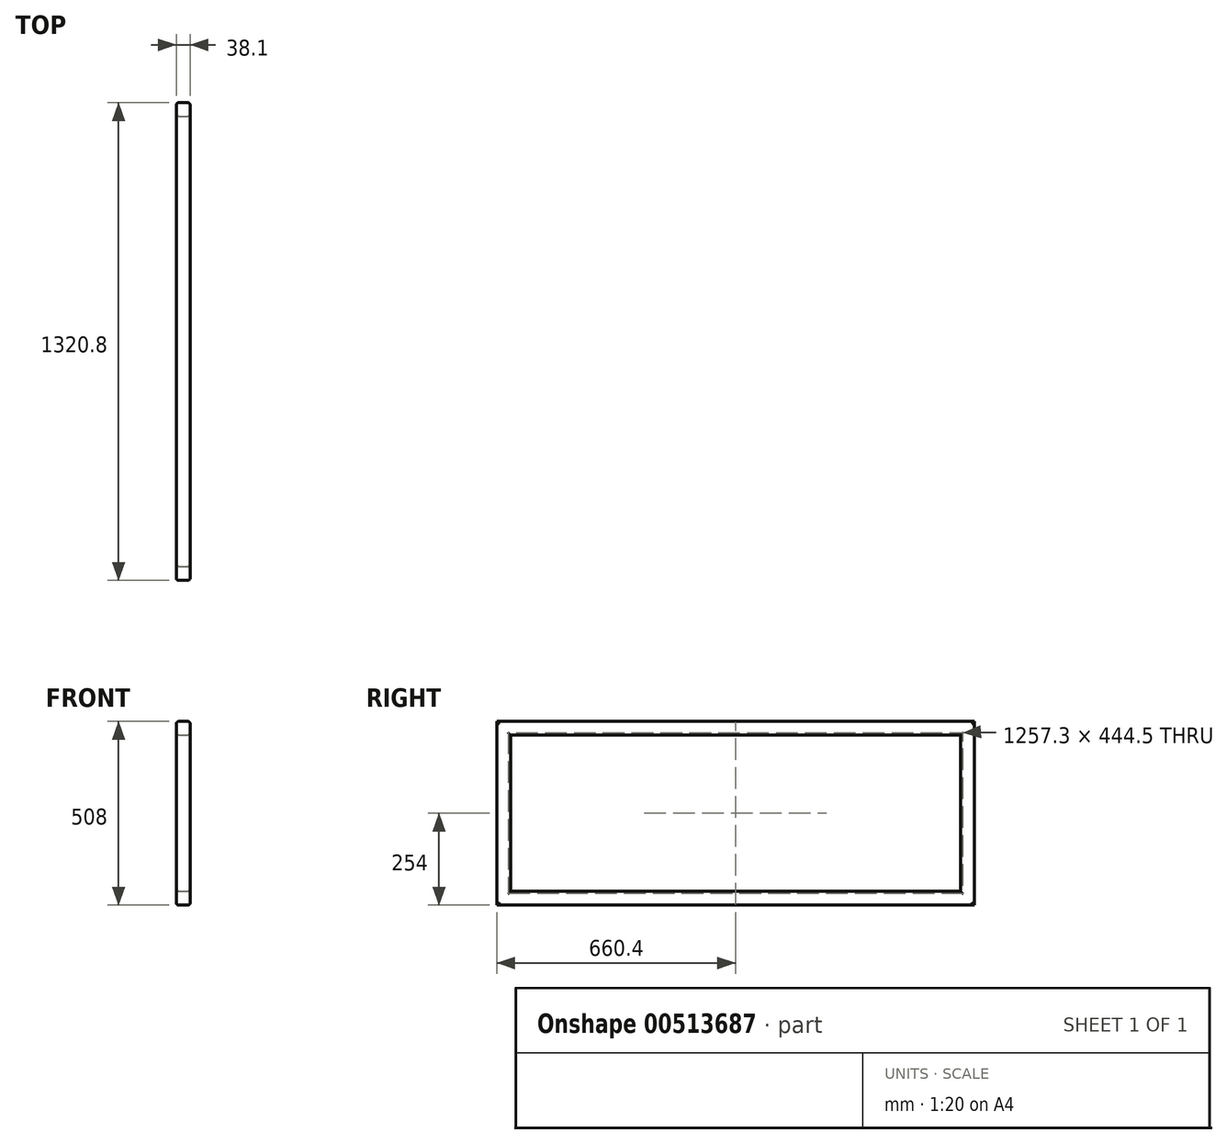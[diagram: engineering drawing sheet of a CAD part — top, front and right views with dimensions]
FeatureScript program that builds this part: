
annotation { "Feature Type Name" : "Feature", "Feature Type Description" : "" }
export const myFeature = defineFeature(function(context is Context, id is Id, definition is map)
    precondition{}
    {
        {
            var Q0;
            Q0=qCreatedBy(makeId("Right.planeOp"),FACE);
            var sketch = newSketch(context, id + "F0", { "sketchPlane" : qUnion([Q0])});
            skLineSegment(sketch, "E0.bottom", {"start": v(-660.4, 254) * mm, "end": v(660.4, 254) * mm});
            skLineSegment(sketch, "E0.top", {"start": v(-660.4, -254) * mm, "end": v(660.4, -254) * mm});
            skLineSegment(sketch, "E0.left", {"start": v(-660.4, 254) * mm, "end": v(-660.4, -254) * mm});
            skLineSegment(sketch, "E0.right", {"start": v(660.4, 254) * mm, "end": v(660.4, -254) * mm});
            skPoint(sketch, "E0.middle", {"position": v(0, 0) * mm});
            skSolve(sketch);
        }
        {
            var Q0;
            Q0=qCreatedBy(makeId("Front.planeOp"),FACE);
            var sketch = newSketch(context, id + "F1", { "sketchPlane" : qUnion([Q0])});
            skPoint(sketch, "E1.0", {"position": v(0, -254) * mm});
            skLineSegment(sketch, "E2", {"start": v(0, -254) * mm, "end": v(-12.7, -254) * mm});
            skLineSegment(sketch, "E3", {"start": v(-19.05, -247.65) * mm, "end": v(-19.05, -222.25) * mm});
            skLineSegment(sketch, "E4", {"start": v(-12.7, -215.9) * mm, "end": v(0, -215.9) * mm});
            skLineSegment(sketch, "E5.0", {"start": v(-12.7, -219.08) * mm, "end": v(0, -219.08) * mm});
            skLineSegment(sketch, "E5.1", {"start": v(-15.88, -247.65) * mm, "end": v(-15.88, -222.25) * mm});
            skLineSegment(sketch, "E5.2", {"start": v(0, -250.83) * mm, "end": v(-12.7, -250.83) * mm});
            skPoint(sketch, "E6.visualSharp", {"position": v(-15.88, -219.08) * mm});
            skArc(sketch, "E6.filletArc", {"start": v(-12.7, -219.08) * mm, "mid": v(-14.95, -220) * mm, "end": v(-15.88, -222.25) * mm});
            skPoint(sketch, "E7.visualSharp", {"position": v(-15.88, -250.83) * mm});
            skArc(sketch, "E7.filletArc", {"start": v(-15.88, -247.65) * mm, "mid": v(-14.95, -249.9) * mm, "end": v(-12.7, -250.83) * mm});
            skPoint(sketch, "E8.visualSharp", {"position": v(-19.05, -215.9) * mm});
            skArc(sketch, "E8.filletArc", {"start": v(-12.7, -215.9) * mm, "mid": v(-17.2, -217.76) * mm, "end": v(-19.05, -222.25) * mm});
            skPoint(sketch, "E9.visualSharp", {"position": v(-19.05, -254) * mm});
            skArc(sketch, "E9.filletArc", {"start": v(-19.05, -247.65) * mm, "mid": v(-17.2, -252.14) * mm, "end": v(-12.7, -254) * mm});
            skLineSegment(sketch, "E10", {"start": v(0, -266.73) * mm, "end": v(0, -188.29) * mm, "construction": true});
            skArc(sketch, "E11.MirrorCS", {"start": v(15.88, -247.65) * mm, "mid": v(14.95, -249.9) * mm, "end": v(12.7, -250.83) * mm});
            skArc(sketch, "E12.MirrorCS", {"start": v(12.7, -219.08) * mm, "mid": v(14.95, -220) * mm, "end": v(15.88, -222.25) * mm});
            skLineSegment(sketch, "E13.MirrorCS", {"start": v(0, -250.83) * mm, "end": v(12.7, -250.83) * mm});
            skLineSegment(sketch, "E14.MirrorCS", {"start": v(0, -254) * mm, "end": v(12.7, -254) * mm});
            skArc(sketch, "E15.MirrorCS", {"start": v(12.7, -215.9) * mm, "mid": v(17.2, -217.76) * mm, "end": v(19.05, -222.25) * mm});
            skArc(sketch, "E16.MirrorCS", {"start": v(19.05, -247.65) * mm, "mid": v(17.2, -252.14) * mm, "end": v(12.7, -254) * mm});
            skPoint(sketch, "E17.MirrorP", {"position": v(19.05, -254) * mm});
            skLineSegment(sketch, "E18.MirrorCS", {"start": v(15.88, -247.65) * mm, "end": v(15.88, -222.25) * mm});
            skLineSegment(sketch, "E19.MirrorCS", {"start": v(12.7, -219.08) * mm, "end": v(0, -219.08) * mm});
            skPoint(sketch, "E20.MirrorP", {"position": v(15.88, -219.08) * mm});
            skPoint(sketch, "E21.MirrorP", {"position": v(15.88, -250.83) * mm});
            skLineSegment(sketch, "E22.MirrorCS", {"start": v(19.05, -247.65) * mm, "end": v(19.05, -222.25) * mm});
            skLineSegment(sketch, "E23.MirrorCS", {"start": v(12.7, -215.9) * mm, "end": v(0, -215.9) * mm});
            skPoint(sketch, "E24.MirrorP", {"position": v(19.05, -215.9) * mm});
            skSolve(sketch);
        }
        {
            var Q0;
            Q0=makeQuery(id+"F1.imprint","IMPRINT",FACE,{"disambiguationData":[TD([[makeQuery(id+"F1.imprint","IMPRINT",EDGE,{"derivedFrom":sQuery(id+"F1.wireOp",EDGE,"E5.0")}),-1.0]])]});
            var Q1;
            Q1=makeQuery(id+"F1.imprint","IMPRINT",FACE,{"disambiguationData":[TD([[makeQuery(id+"F1.imprint","IMPRINT",EDGE,{"derivedFrom":sQuery(id+"F1.wireOp",EDGE,"E2")}),-1.0]])]});
            var Q2;
            Q2=sQuery(id+"F0.wireOp",EDGE,"E0.top");
            var Q3;
            Q3=sQuery(id+"F0.wireOp",EDGE,"E0.right");
            var Q4;
            Q4=sQuery(id+"F0.wireOp",EDGE,"E0.bottom");
            var Q5;
            Q5=sQuery(id+"F0.wireOp",EDGE,"E0.left");
            sweep(context, id + "F2", {"profiles" : qUnion([Q0, Q1]), "path" : qUnion([Q2, Q3, Q4, Q5])});
        }
    });
